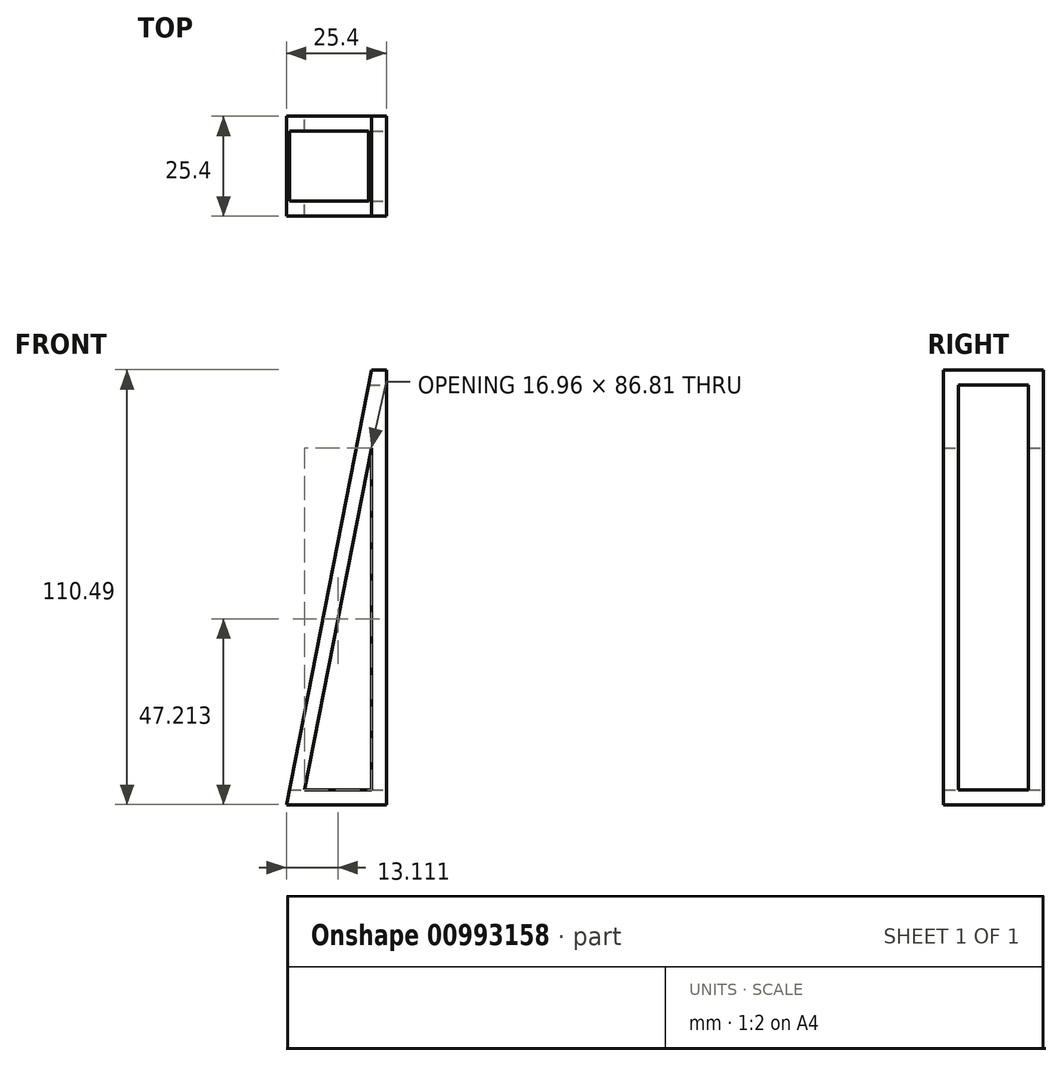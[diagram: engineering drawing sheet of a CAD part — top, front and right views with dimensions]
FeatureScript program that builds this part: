
annotation { "Feature Type Name" : "Feature", "Feature Type Description" : "" }
export const myFeature = defineFeature(function(context is Context, id is Id, definition is map)
    precondition{}
    {
        {
            var Q0;
            Q0=qCreatedBy(makeId("Front.planeOp"),FACE);
            var sketch = newSketch(context, id + "F0", { "sketchPlane" : qUnion([Q0])});
            skLineSegment(sketch, "E0", {"start": v(-30.45, 76.34) * mm, "end": v(-52.04, -34.15) * mm});
            skLineSegment(sketch, "E1", {"start": v(-52.04, -34.15) * mm, "end": v(-26.64, -34.15) * mm});
            skLineSegment(sketch, "E2", {"start": v(-26.64, -34.15) * mm, "end": v(-26.64, 76.34) * mm});
            skLineSegment(sketch, "E3", {"start": v(-26.64, 76.34) * mm, "end": v(-30.45, 76.34) * mm});
            skLineSegment(sketch, "E4", {"start": v(-30.45, 56.47) * mm, "end": v(-30.45, -30.34) * mm});
            skLineSegment(sketch, "E5", {"start": v(-30.45, -30.34) * mm, "end": v(-47.41, -30.34) * mm});
            skLineSegment(sketch, "E6", {"start": v(-47.41, -30.34) * mm, "end": v(-30.45, 56.47) * mm});
            skSolve(sketch);
        }
        {
            var Q0;
            Q0=makeQuery(id+"F0.imprint","IMPRINT",FACE,{"disambiguationData":[TD([[makeQuery(id+"F0.imprint","IMPRINT",EDGE,{"derivedFrom":sQuery(id+"F0.wireOp",EDGE,"E0")}),1.0]])]});
            extrude(context, id + "F1", {"entities" : qUnion([Q0]), "depth" : 25.4 * mm, "offsetDistance" : 25.4 * mm});
        }
        {
            var Q0;
            Q0=makeQuery(id+"F1.opExtrude","SWEPT_FACE",FACE,{"disambiguationData":[OSD([sQuery(id+"F0.wireOp",EDGE,"E2")])]});
            var sketch = newSketch(context, id + "F2", { "sketchPlane" : qUnion([Q0])});
            skLineSegment(sketch, "E7.bottom", {"start": v(-21.6, 72.53) * mm, "end": v(-3.81, 72.53) * mm});
            skLineSegment(sketch, "E7.top", {"start": v(-21.59, -30.34) * mm, "end": v(-3.8, -30.34) * mm});
            skLineSegment(sketch, "E7.left", {"start": v(-21.6, 72.53) * mm, "end": v(-21.6, -30.34) * mm});
            skLineSegment(sketch, "E7.right", {"start": v(-3.81, 72.53) * mm, "end": v(-3.81, -30.34) * mm});
            skSolve(sketch);
        }
        {
            var Q0;
            Q0=makeQuery(id+"F2.imprint","IMPRINT",FACE,{"disambiguationData":[TD([[makeQuery(id+"F2.imprint","IMPRINT",EDGE,{"derivedFrom":sQuery(id+"F2.wireOp",EDGE,"E7.bottom")}),-1.0]])]});
            extrude(context, id + "F3", {"entities" : qUnion([Q0]), "operationType" : NewBodyOperationType.REMOVE, "oppositeDirection" : true, "depth" : 50.8 * mm, "offsetDistance" : 25.4 * mm});
        }
    });
